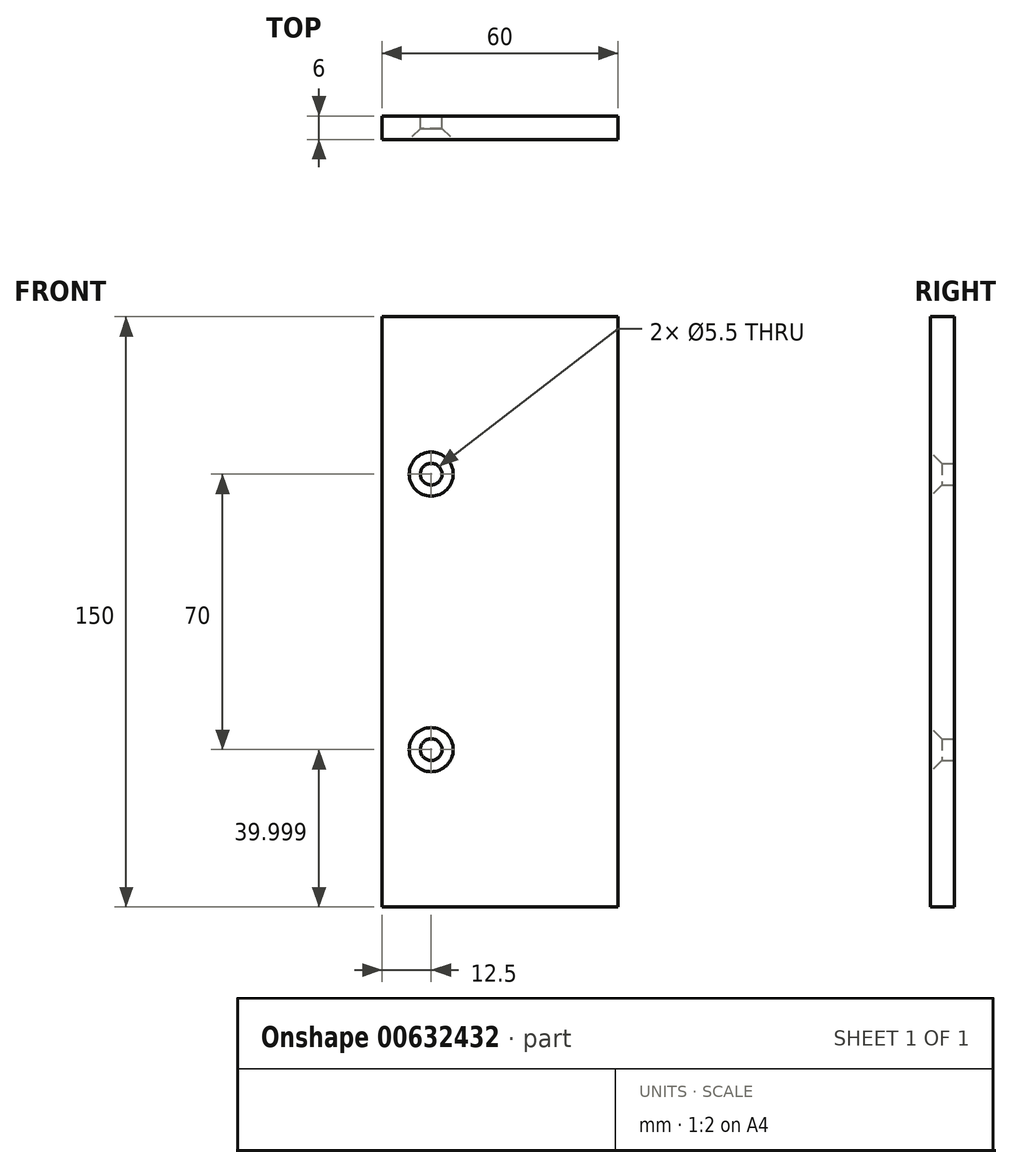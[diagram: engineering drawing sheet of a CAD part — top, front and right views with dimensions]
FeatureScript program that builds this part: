
annotation { "Feature Type Name" : "Feature", "Feature Type Description" : "" }
export const myFeature = defineFeature(function(context is Context, id is Id, definition is map)
    precondition{}
    {
        {
            var Q0;
            Q0=qCreatedBy(makeId("Front.planeOp"),FACE);
            var sketch = newSketch(context, id + "F0", { "sketchPlane" : qUnion([Q0])});
            skLineSegment(sketch, "E0.bottom", {"start": v(0, 86.55) * mm, "end": v(60, 86.55) * mm});
            skLineSegment(sketch, "E0.top", {"start": v(0, -63.45) * mm, "end": v(60, -63.45) * mm});
            skLineSegment(sketch, "E0.left", {"start": v(0, 86.55) * mm, "end": v(0, -63.45) * mm});
            skLineSegment(sketch, "E0.right", {"start": v(60, 86.55) * mm, "end": v(60, -63.45) * mm});
            skPoint(sketch, "E1", {"position": v(12.5, 46.55) * mm});
            skPoint(sketch, "E2", {"position": v(12.5, -23.45) * mm});
            skLineSegment(sketch, "E3", {"start": v(60, 11.55) * mm, "end": v(0, 11.55) * mm, "construction": true});
            skSolve(sketch);
        }
        {
            var Q0;
            Q0=makeQuery(id+"F0.imprint","IMPRINT",FACE,{"disambiguationData":[TD([[makeQuery(id+"F0.imprint","IMPRINT",EDGE,{"derivedFrom":sQuery(id+"F0.wireOp",EDGE,"E0.bottom")}),-1.0]])]});
            extrude(context, id + "F1", {"entities" : qUnion([Q0]), "oppositeDirection" : true, "depth" : 6 * mm, "offsetDistance" : 25 * mm});
        }
        {
            var Q0;
            Q0=sQuery(id+"F0.wireOp",VERTEX,"E1");
            var Q1;
            Q1=sQuery(id+"F0.wireOp",VERTEX,"E2");
            var Q2;
            Q2=makeQuery(id+"F1.opExtrude","SWEPT_BODY",BODY,{"disambiguationData":[OSD([sQuery(id+"F0.wireOp",EDGE,"E0.bottom"),sQuery(id+"F0.wireOp",EDGE,"E0.top"),sQuery(id+"F0.wireOp",EDGE,"E0.left"),sQuery(id+"F0.wireOp",EDGE,"E0.right")])]});
            hole(context, id + "F2", {"style" : HoleStyle.C_SINK, "endStyle" : HoleEndStyle.THROUGH, "standardTappedOrClearance" : lookupTablePath({ "standard" : "ISO", "fit" : "Normal", "size" : "M5", "type" : "Clearance" }), "standardBlindInLast" : lookupTablePath({ "fit" : "Standard", "standard" : "ISO", "size" : "M5", "type" : "Clearance" }), "holeDiameter" : 5.5 * mm, "cSinkDiameter" : 11.2 * mm, "cSinkAngle" : 90 * degree, "majorDiameter" : 5 * mm, "isTappedThrough" : true, "tappedDepth" : 12 * mm, "tapClearance" : 3, "startFromSketch" : true, "locations" : qUnion([Q0, Q1]), "scope" : qUnion([Q2])});
        }
    });
